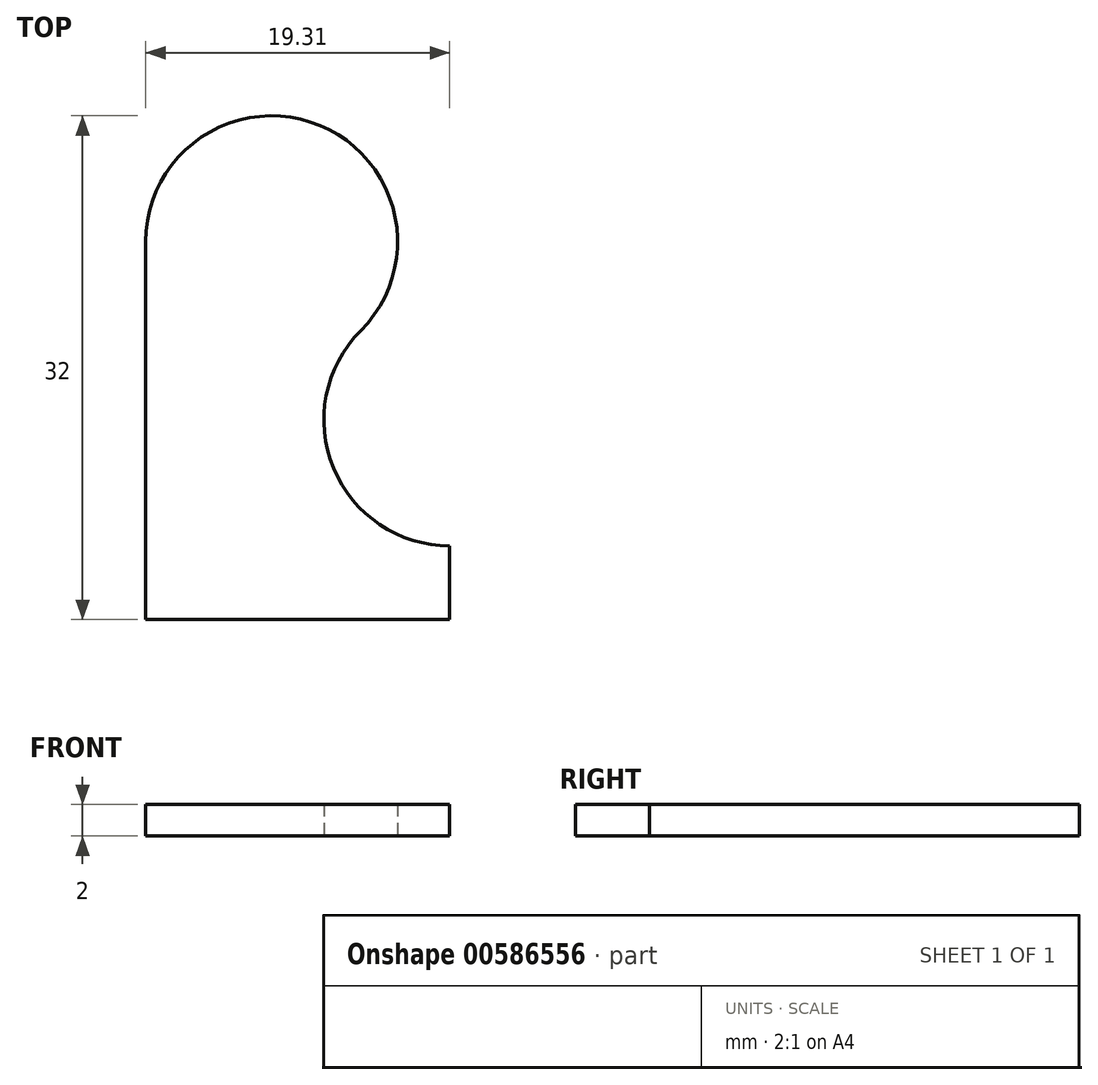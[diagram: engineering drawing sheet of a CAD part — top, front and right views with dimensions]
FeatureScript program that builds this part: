
annotation { "Feature Type Name" : "Feature", "Feature Type Description" : "" }
export const myFeature = defineFeature(function(context is Context, id is Id, definition is map)
    precondition{}
    {
        {
            var Q0;
            Q0=qCreatedBy(makeId("Top.planeOp"),FACE);
            var sketch = newSketch(context, id + "F0", { "sketchPlane" : qUnion([Q0])});
            skLineSegment(sketch, "E0", {"start": v(0, 0) * mm, "end": v(0, 24) * mm});
            skArc(sketch, "E1", {"start": v(0, 24) * mm, "mid": v(11.06, 31.4) * mm, "end": v(13.66, 18.34) * mm});
            skArc(sketch, "E2", {"start": v(13.66, 18.34) * mm, "mid": v(11.92, 9.62) * mm, "end": v(19.31, 4.69) * mm});
            skLineSegment(sketch, "E3", {"start": v(8, 24) * mm, "end": v(19.31, 12.69) * mm, "construction": true});
            skLineSegment(sketch, "E4", {"start": v(19.31, 0) * mm, "end": v(19.31, 12.69) * mm, "construction": true});
            skLineSegment(sketch, "E5", {"start": v(0, 0) * mm, "end": v(19.31, 0) * mm});
            skLineSegment(sketch, "E6", {"start": v(19.31, 4.69) * mm, "end": v(19.31, 0) * mm});
            skLineSegment(sketch, "E7", {"start": v(0, 24) * mm, "end": v(8, 24) * mm, "construction": true});
            skLineSegment(sketch, "E8", {"start": v(8, 24) * mm, "end": v(8, 16) * mm, "construction": true});
            skLineSegment(sketch, "E9", {"start": v(8, 16) * mm, "end": v(8, 8) * mm, "construction": true});
            skLineSegment(sketch, "E10", {"start": v(8, 0) * mm, "end": v(8, 8) * mm, "construction": true});
            skSolve(sketch);
        }
        {
            var Q0;
            Q0=qSketchRegion(id+"F0",true);
            extrude(context, id + "F1", {"entities" : qUnion([Q0]), "depth" : 2 * mm, "offsetDistance" : 25 * mm});
        }
    });
